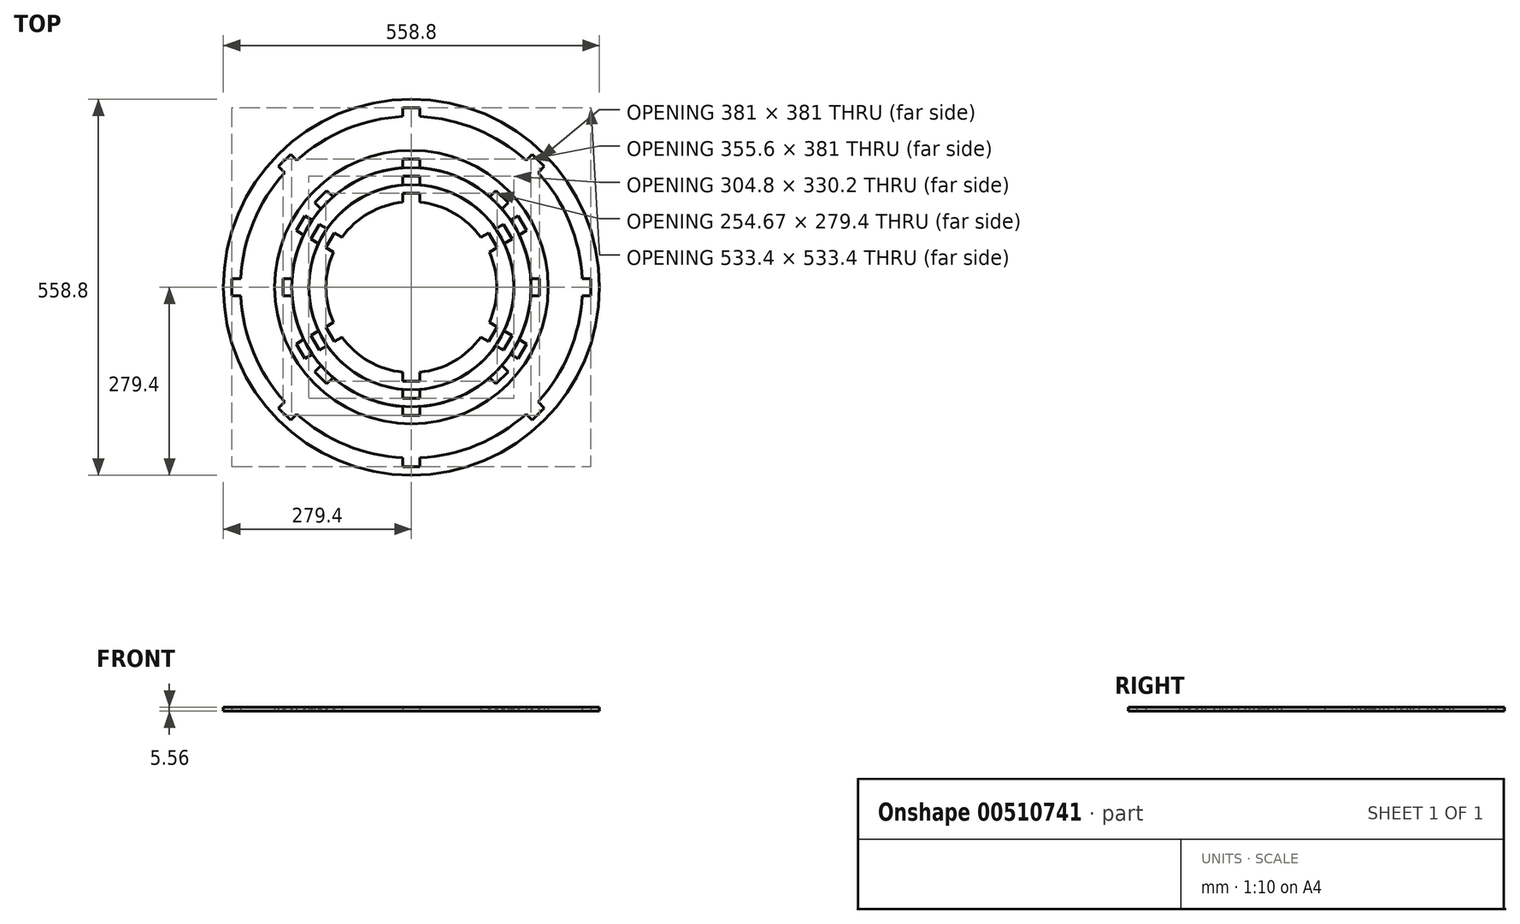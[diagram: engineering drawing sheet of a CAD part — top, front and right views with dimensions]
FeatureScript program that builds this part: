
annotation { "Feature Type Name" : "Feature", "Feature Type Description" : "" }
export const myFeature = defineFeature(function(context is Context, id is Id, definition is map)
    precondition{}
    {
        {
            var Q0;
            Q0=qCreatedBy(makeId("Top.planeOp"),FACE);
            var sketch = newSketch(context, id + "F0", { "sketchPlane" : qUnion([Q0])});
            skCircle(sketch, "E0", {"center": v(0, 0) * mm, "radius": 127 * mm});
            skCircle(sketch, "E1", {"center": v(0, 0) * mm, "radius": 152.4 * mm});
            skCircle(sketch, "E2", {"center": v(0, 0) * mm, "radius": 177.8 * mm});
            skCircle(sketch, "E3.cCircle", {"center": v(0, 0) * mm, "radius": 139.7 * mm, "construction": true});
            skLineSegment(sketch, "E3.0", {"start": v(-80.66, 139.7) * mm, "end": v(80.66, 139.7) * mm, "construction": true});
            skLineSegment(sketch, "E3.1", {"start": v(80.66, 139.7) * mm, "end": v(161.31, 0) * mm, "construction": true});
            skLineSegment(sketch, "E3.2", {"start": v(161.31, 0) * mm, "end": v(80.66, -139.7) * mm, "construction": true});
            skLineSegment(sketch, "E3.4", {"start": v(-80.66, -139.7) * mm, "end": v(-161.31, 0) * mm, "construction": true});
            skLineSegment(sketch, "E3.5", {"start": v(-161.31, 0) * mm, "end": v(-80.66, 139.7) * mm, "construction": true});
            skPoint(sketch, "E3.0.midPoint", {"position": v(0, 139.7) * mm});
            skCircle(sketch, "E4.cCircle", {"center": v(0, 0) * mm, "radius": 165.1 * mm, "construction": true});
            skLineSegment(sketch, "E4.0", {"start": v(-95.32, 165.1) * mm, "end": v(95.32, 165.1) * mm, "construction": true});
            skLineSegment(sketch, "E4.1", {"start": v(95.32, 165.1) * mm, "end": v(190.64, 0) * mm, "construction": true});
            skLineSegment(sketch, "E4.2", {"start": v(190.64, 0) * mm, "end": v(95.32, -165.1) * mm, "construction": true});
            skLineSegment(sketch, "E4.4", {"start": v(-95.32, -165.1) * mm, "end": v(-190.64, 0) * mm, "construction": true});
            skLineSegment(sketch, "E4.5", {"start": v(-190.64, 0) * mm, "end": v(-95.32, 165.1) * mm, "construction": true});
            skPoint(sketch, "E4.0.midPoint", {"position": v(0, 165.1) * mm});
            skCircle(sketch, "E5.cCircle", {"center": v(0, 0) * mm, "radius": 190.5 * mm, "construction": true});
            skLineSegment(sketch, "E5.0", {"start": v(-109.99, 190.5) * mm, "end": v(109.99, 190.5) * mm, "construction": true});
            skLineSegment(sketch, "E5.1", {"start": v(109.99, 190.5) * mm, "end": v(219.97, 0) * mm, "construction": true});
            skLineSegment(sketch, "E5.2", {"start": v(219.97, 0) * mm, "end": v(109.99, -190.5) * mm, "construction": true});
            skLineSegment(sketch, "E5.4", {"start": v(-109.99, -190.5) * mm, "end": v(-219.97, 0) * mm, "construction": true});
            skLineSegment(sketch, "E5.5", {"start": v(-219.97, 0) * mm, "end": v(-109.99, 190.5) * mm, "construction": true});
            skPoint(sketch, "E5.0.midPoint", {"position": v(0, 190.5) * mm});
            skCircle(sketch, "E6", {"center": v(0, 0) * mm, "radius": 203.2 * mm});
            skLineSegment(sketch, "E7", {"start": v(0, 114.9) * mm, "end": v(12.7, 114.9) * mm, "construction": true});
            skLineSegment(sketch, "E8", {"start": v(12.7, 126.36) * mm, "end": v(12.7, 139.7) * mm});
            skLineSegment(sketch, "E9", {"start": v(12.7, 139.7) * mm, "end": v(-12.7, 139.7) * mm});
            skLineSegment(sketch, "E10", {"start": v(-12.7, 139.7) * mm, "end": v(-12.7, 126.36) * mm});
            skLineSegment(sketch, "E11", {"start": v(-12.7, 151.87) * mm, "end": v(-12.7, 164.61) * mm});
            skLineSegment(sketch, "E12", {"start": v(-12.7, 164.61) * mm, "end": v(-12.7, 165.1) * mm});
            skLineSegment(sketch, "E13", {"start": v(-12.7, 165.1) * mm, "end": v(12.7, 165.1) * mm});
            skLineSegment(sketch, "E14", {"start": v(12.7, 165.1) * mm, "end": v(12.7, 151.87) * mm});
            skLineSegment(sketch, "E15", {"start": v(-12.7, 177.35) * mm, "end": v(-12.7, 190.5) * mm});
            skLineSegment(sketch, "E16", {"start": v(-12.7, 190.5) * mm, "end": v(12.7, 190.5) * mm});
            skLineSegment(sketch, "E17", {"start": v(12.7, 190.5) * mm, "end": v(12.7, 177.35) * mm});
            skPoint(sketch, "E18.orphan", {"position": v(-12.7, 120.26) * mm});
            skPoint(sketch, "E19.center", {"position": v(0.37, 0.77) * mm});
            skPoint(sketch, "E20.1.0", {"position": v(-164.98, 95.25) * mm});
            skLineSegment(sketch, "E20.1.1", {"start": v(-159.94, 77.67) * mm, "end": v(-171.33, 84.25) * mm});
            skLineSegment(sketch, "E20.1.2", {"start": v(-103.08, 74.18) * mm, "end": v(-114.63, 80.85) * mm});
            skLineSegment(sketch, "E20.1.3", {"start": v(-171.33, 84.25) * mm, "end": v(-158.63, 106.25) * mm});
            skLineSegment(sketch, "E20.1.4", {"start": v(-149.33, 71.55) * mm, "end": v(-136.63, 93.55) * mm});
            skLineSegment(sketch, "E20.1.5", {"start": v(-127.33, 58.85) * mm, "end": v(-115.78, 52.18) * mm});
            skLineSegment(sketch, "E20.1.6", {"start": v(-136.63, 93.55) * mm, "end": v(-125.17, 86.93) * mm});
            skPoint(sketch, "E20.1.7", {"position": v(-120.98, 69.85) * mm});
            skPoint(sketch, "E20.1.8", {"position": v(-142.98, 82.55) * mm});
            skLineSegment(sketch, "E20.1.9", {"start": v(-137.87, 64.94) * mm, "end": v(-148.9, 71.3) * mm});
            skLineSegment(sketch, "E20.1.10", {"start": v(-114.63, 80.85) * mm, "end": v(-127.33, 58.85) * mm});
            skLineSegment(sketch, "E20.1.11", {"start": v(-158.63, 106.25) * mm, "end": v(-147.24, 99.67) * mm});
            skLineSegment(sketch, "E20.1.12", {"start": v(-148.9, 71.3) * mm, "end": v(-149.33, 71.55) * mm});
            skPoint(sketch, "E20.2.0", {"position": v(-164.98, -95.25) * mm});
            skLineSegment(sketch, "E20.2.1", {"start": v(-147.24, -99.67) * mm, "end": v(-158.63, -106.25) * mm});
            skLineSegment(sketch, "E20.2.2", {"start": v(-115.78, -52.18) * mm, "end": v(-127.33, -58.85) * mm});
            skLineSegment(sketch, "E20.2.3", {"start": v(-158.63, -106.25) * mm, "end": v(-171.33, -84.25) * mm});
            skLineSegment(sketch, "E20.2.4", {"start": v(-136.63, -93.55) * mm, "end": v(-149.33, -71.55) * mm});
            skLineSegment(sketch, "E20.2.5", {"start": v(-114.63, -80.85) * mm, "end": v(-103.08, -74.18) * mm});
            skLineSegment(sketch, "E20.2.6", {"start": v(-149.33, -71.55) * mm, "end": v(-137.87, -64.94) * mm});
            skPoint(sketch, "E20.2.7", {"position": v(-120.98, -69.85) * mm});
            skPoint(sketch, "E20.2.8", {"position": v(-142.98, -82.55) * mm});
            skLineSegment(sketch, "E20.2.9", {"start": v(-125.17, -86.93) * mm, "end": v(-136.2, -93.3) * mm});
            skLineSegment(sketch, "E20.2.10", {"start": v(-127.33, -58.85) * mm, "end": v(-114.63, -80.85) * mm});
            skLineSegment(sketch, "E20.2.11", {"start": v(-171.33, -84.25) * mm, "end": v(-159.94, -77.67) * mm});
            skLineSegment(sketch, "E20.2.12", {"start": v(-136.2, -93.3) * mm, "end": v(-136.63, -93.55) * mm});
            skPoint(sketch, "E20.3.0", {"position": v(0, -190.5) * mm});
            skLineSegment(sketch, "E20.3.1", {"start": v(12.7, -177.35) * mm, "end": v(12.7, -190.5) * mm});
            skLineSegment(sketch, "E20.3.2", {"start": v(-12.7, -126.36) * mm, "end": v(-12.7, -139.7) * mm});
            skLineSegment(sketch, "E20.3.3", {"start": v(12.7, -190.5) * mm, "end": v(-12.7, -190.5) * mm});
            skLineSegment(sketch, "E20.3.4", {"start": v(12.7, -165.1) * mm, "end": v(-12.7, -165.1) * mm});
            skLineSegment(sketch, "E20.3.5", {"start": v(12.7, -139.7) * mm, "end": v(12.7, -126.36) * mm});
            skLineSegment(sketch, "E20.3.6", {"start": v(-12.7, -165.1) * mm, "end": v(-12.7, -151.87) * mm});
            skPoint(sketch, "E20.3.7", {"position": v(0, -139.7) * mm});
            skPoint(sketch, "E20.3.8", {"position": v(0, -165.1) * mm});
            skLineSegment(sketch, "E20.3.9", {"start": v(12.7, -151.87) * mm, "end": v(12.7, -164.61) * mm});
            skLineSegment(sketch, "E20.3.10", {"start": v(-12.7, -139.7) * mm, "end": v(12.7, -139.7) * mm});
            skLineSegment(sketch, "E20.3.11", {"start": v(-12.7, -190.5) * mm, "end": v(-12.7, -177.35) * mm});
            skLineSegment(sketch, "E20.3.12", {"start": v(12.7, -164.61) * mm, "end": v(12.7, -165.1) * mm});
            skPoint(sketch, "E20.4.0", {"position": v(164.98, -95.25) * mm});
            skLineSegment(sketch, "E20.4.1", {"start": v(159.94, -77.67) * mm, "end": v(171.33, -84.25) * mm});
            skLineSegment(sketch, "E20.4.2", {"start": v(103.08, -74.18) * mm, "end": v(114.63, -80.85) * mm});
            skLineSegment(sketch, "E20.4.3", {"start": v(171.33, -84.25) * mm, "end": v(158.63, -106.25) * mm});
            skLineSegment(sketch, "E20.4.4", {"start": v(149.33, -71.55) * mm, "end": v(136.63, -93.55) * mm});
            skLineSegment(sketch, "E20.4.5", {"start": v(127.33, -58.85) * mm, "end": v(115.78, -52.18) * mm});
            skLineSegment(sketch, "E20.4.6", {"start": v(136.63, -93.55) * mm, "end": v(125.17, -86.93) * mm});
            skPoint(sketch, "E20.4.7", {"position": v(120.98, -69.85) * mm});
            skPoint(sketch, "E20.4.8", {"position": v(142.98, -82.55) * mm});
            skLineSegment(sketch, "E20.4.9", {"start": v(137.87, -64.94) * mm, "end": v(148.9, -71.3) * mm});
            skLineSegment(sketch, "E20.4.10", {"start": v(114.63, -80.85) * mm, "end": v(127.33, -58.85) * mm});
            skLineSegment(sketch, "E20.4.11", {"start": v(158.63, -106.25) * mm, "end": v(147.24, -99.67) * mm});
            skLineSegment(sketch, "E20.4.12", {"start": v(148.9, -71.3) * mm, "end": v(149.33, -71.55) * mm});
            skPoint(sketch, "E20.5.0", {"position": v(164.98, 95.25) * mm});
            skLineSegment(sketch, "E20.5.1", {"start": v(147.24, 99.67) * mm, "end": v(158.63, 106.25) * mm});
            skLineSegment(sketch, "E20.5.2", {"start": v(115.78, 52.18) * mm, "end": v(127.33, 58.85) * mm});
            skLineSegment(sketch, "E20.5.3", {"start": v(158.63, 106.25) * mm, "end": v(171.33, 84.25) * mm});
            skLineSegment(sketch, "E20.5.4", {"start": v(136.63, 93.55) * mm, "end": v(149.33, 71.55) * mm});
            skLineSegment(sketch, "E20.5.5", {"start": v(114.63, 80.85) * mm, "end": v(103.08, 74.18) * mm});
            skLineSegment(sketch, "E20.5.6", {"start": v(149.33, 71.55) * mm, "end": v(137.87, 64.94) * mm});
            skPoint(sketch, "E20.5.7", {"position": v(120.98, 69.85) * mm});
            skPoint(sketch, "E20.5.8", {"position": v(142.98, 82.55) * mm});
            skLineSegment(sketch, "E20.5.9", {"start": v(125.17, 86.93) * mm, "end": v(136.2, 93.3) * mm});
            skLineSegment(sketch, "E20.5.10", {"start": v(127.33, 58.85) * mm, "end": v(114.63, 80.85) * mm});
            skLineSegment(sketch, "E20.5.11", {"start": v(171.33, 84.25) * mm, "end": v(159.94, 77.67) * mm});
            skLineSegment(sketch, "E20.5.12", {"start": v(136.2, 93.3) * mm, "end": v(136.63, 93.55) * mm});
            skSolve(sketch);
        }
        {
            var Q0;
            {var subQ17=sQuery(id+"F0.wireOp",EDGE,"E8");Q0=makeQuery(id+"F0.imprint","IMPRINT",FACE,{"disambiguationData":[TD([[makeQuery(id+"F0.imprint","IMPRINT",EDGE,{"derivedFrom":subQ17}),-1.0]])]});}
            var Q1;
            Q1=makeQuery(id+"F0.imprint","IMPRINT",FACE,{"disambiguationData":[TD([[makeQuery(id+"F0.imprint","IMPRINT",EDGE,{"derivedFrom":sQuery(id+"F0.wireOp",EDGE,"E6")}),1.0]])]});
            extrude(context, id + "F1", {"entities" : qUnion([Q0, Q1]), "depth" : 5.56 * mm, "offsetDistance" : 25.4 * mm});
        }
        {
            var Q0;
            {var subQ16=sQuery(id+"F0.wireOp",EDGE,"E11");Q0=makeQuery(id+"F0.imprint","IMPRINT",FACE,{"disambiguationData":[TD([[makeQuery(id+"F0.imprint","IMPRINT",EDGE,{"derivedFrom":subQ16}),1.0]])]});}
            extrude(context, id + "F2", {"entities" : qUnion([Q0]), "depth" : 5.56 * mm, "offsetDistance" : 25.4 * mm});
        }
        {
            var Q0;
            Q0=qCreatedBy(makeId("Top.planeOp"),FACE);
            var sketch = newSketch(context, id + "F3", { "sketchPlane" : qUnion([Q0])});
            skCircle(sketch, "E21", {"center": v(0, 0) * mm, "radius": 177.8 * mm});
            skCircle(sketch, "E22", {"center": v(0, 0) * mm, "radius": 203.2 * mm});
            skCircle(sketch, "E23.cCircle", {"center": v(0, 0) * mm, "radius": 190.5 * mm, "construction": true});
            skLineSegment(sketch, "E23.0", {"start": v(-78.9, 190.5) * mm, "end": v(78.9, 190.5) * mm, "construction": true});
            skLineSegment(sketch, "E23.1", {"start": v(78.9, 190.5) * mm, "end": v(190.5, 78.9) * mm, "construction": true});
            skLineSegment(sketch, "E23.2", {"start": v(190.5, 78.9) * mm, "end": v(190.5, -78.9) * mm, "construction": true});
            skLineSegment(sketch, "E23.3", {"start": v(190.5, -78.9) * mm, "end": v(78.9, -190.5) * mm, "construction": true});
            skLineSegment(sketch, "E23.4", {"start": v(78.9, -190.5) * mm, "end": v(-78.9, -190.5) * mm, "construction": true});
            skLineSegment(sketch, "E23.5", {"start": v(-78.9, -190.5) * mm, "end": v(-190.5, -78.9) * mm, "construction": true});
            skLineSegment(sketch, "E23.6", {"start": v(-190.5, -78.9) * mm, "end": v(-190.5, 78.9) * mm, "construction": true});
            skLineSegment(sketch, "E23.7", {"start": v(-190.5, 78.9) * mm, "end": v(-78.9, 190.5) * mm, "construction": true});
            skPoint(sketch, "E23.0.midPoint", {"position": v(0, 190.5) * mm});
            skLineSegment(sketch, "E24", {"start": v(0, 190.5) * mm, "end": v(12.7, 190.5) * mm});
            skLineSegment(sketch, "E25", {"start": v(12.7, 190.5) * mm, "end": v(12.7, 177.35) * mm});
            skLineSegment(sketch, "E26", {"start": v(0, 190.5) * mm, "end": v(-12.7, 190.5) * mm});
            skLineSegment(sketch, "E27", {"start": v(-12.7, 190.5) * mm, "end": v(-12.7, 177.35) * mm});
            skCircle(sketch, "E28", {"center": v(0, 0) * mm, "radius": 254 * mm});
            skCircle(sketch, "E29", {"center": v(0, 0) * mm, "radius": 279.4 * mm});
            skCircle(sketch, "E30.cCircle", {"center": v(0, 0) * mm, "radius": 266.7 * mm, "construction": true});
            skLineSegment(sketch, "E30.0", {"start": v(-110.47, 266.7) * mm, "end": v(110.47, 266.7) * mm, "construction": true});
            skLineSegment(sketch, "E30.1", {"start": v(110.47, 266.7) * mm, "end": v(266.7, 110.47) * mm, "construction": true});
            skLineSegment(sketch, "E30.2", {"start": v(266.7, 110.47) * mm, "end": v(266.7, -110.47) * mm, "construction": true});
            skLineSegment(sketch, "E30.3", {"start": v(266.7, -110.47) * mm, "end": v(110.47, -266.7) * mm, "construction": true});
            skLineSegment(sketch, "E30.4", {"start": v(110.47, -266.7) * mm, "end": v(-110.47, -266.7) * mm, "construction": true});
            skLineSegment(sketch, "E30.5", {"start": v(-110.47, -266.7) * mm, "end": v(-266.7, -110.47) * mm, "construction": true});
            skLineSegment(sketch, "E30.6", {"start": v(-266.7, -110.47) * mm, "end": v(-266.7, 110.47) * mm, "construction": true});
            skLineSegment(sketch, "E30.7", {"start": v(-266.7, 110.47) * mm, "end": v(-110.47, 266.7) * mm, "construction": true});
            skPoint(sketch, "E30.0.midPoint", {"position": v(0, 266.7) * mm});
            skLineSegment(sketch, "E31", {"start": v(0, 266.7) * mm, "end": v(12.7, 266.7) * mm});
            skLineSegment(sketch, "E32", {"start": v(12.7, 266.7) * mm, "end": v(12.7, 253.68) * mm});
            skLineSegment(sketch, "E33", {"start": v(0, 266.7) * mm, "end": v(-12.7, 266.7) * mm});
            skLineSegment(sketch, "E34", {"start": v(-12.7, 266.7) * mm, "end": v(-12.7, 253.68) * mm});
            skPoint(sketch, "E35.center", {"position": v(0.25, 0.44) * mm});
            skPoint(sketch, "E36.center", {"position": v(0.1, 0.3) * mm});
            skLineSegment(sketch, "E37.1.0", {"start": v(-197.57, 179.6) * mm, "end": v(-188.36, 170.4) * mm});
            skPoint(sketch, "E37.1.1", {"position": v(-188.59, 188.59) * mm});
            skLineSegment(sketch, "E37.1.2", {"start": v(-188.59, 188.59) * mm, "end": v(-179.6, 197.57) * mm});
            skLineSegment(sketch, "E37.1.3", {"start": v(-134.7, 134.7) * mm, "end": v(-125.72, 143.68) * mm});
            skLineSegment(sketch, "E37.1.4", {"start": v(-125.72, 143.68) * mm, "end": v(-116.42, 134.38) * mm});
            skLineSegment(sketch, "E37.1.5", {"start": v(-179.6, 197.57) * mm, "end": v(-170.4, 188.36) * mm});
            skPoint(sketch, "E37.1.6", {"position": v(-134.7, 134.7) * mm});
            skLineSegment(sketch, "E37.1.7", {"start": v(-143.68, 125.72) * mm, "end": v(-134.38, 116.42) * mm});
            skLineSegment(sketch, "E37.1.8", {"start": v(-134.7, 134.7) * mm, "end": v(-143.68, 125.72) * mm});
            skLineSegment(sketch, "E37.1.9", {"start": v(-188.59, 188.59) * mm, "end": v(-197.57, 179.6) * mm});
            skLineSegment(sketch, "E37.2.0", {"start": v(-266.7, -12.7) * mm, "end": v(-253.68, -12.7) * mm});
            skPoint(sketch, "E37.2.1", {"position": v(-266.7, 0) * mm});
            skLineSegment(sketch, "E37.2.2", {"start": v(-266.7, 0) * mm, "end": v(-266.7, 12.7) * mm});
            skLineSegment(sketch, "E37.2.3", {"start": v(-190.5, 0) * mm, "end": v(-190.5, 12.7) * mm});
            skLineSegment(sketch, "E37.2.4", {"start": v(-190.5, 12.7) * mm, "end": v(-177.35, 12.7) * mm});
            skLineSegment(sketch, "E37.2.5", {"start": v(-266.7, 12.7) * mm, "end": v(-253.68, 12.7) * mm});
            skPoint(sketch, "E37.2.6", {"position": v(-190.5, 0) * mm});
            skLineSegment(sketch, "E37.2.7", {"start": v(-190.5, -12.7) * mm, "end": v(-177.35, -12.7) * mm});
            skLineSegment(sketch, "E37.2.8", {"start": v(-190.5, 0) * mm, "end": v(-190.5, -12.7) * mm});
            skLineSegment(sketch, "E37.2.9", {"start": v(-266.7, 0) * mm, "end": v(-266.7, -12.7) * mm});
            skLineSegment(sketch, "E37.3.0", {"start": v(-179.6, -197.57) * mm, "end": v(-170.4, -188.36) * mm});
            skPoint(sketch, "E37.3.1", {"position": v(-188.59, -188.59) * mm});
            skLineSegment(sketch, "E37.3.2", {"start": v(-188.59, -188.59) * mm, "end": v(-197.57, -179.6) * mm});
            skLineSegment(sketch, "E37.3.3", {"start": v(-134.7, -134.7) * mm, "end": v(-143.68, -125.72) * mm});
            skLineSegment(sketch, "E37.3.4", {"start": v(-143.68, -125.72) * mm, "end": v(-134.38, -116.42) * mm});
            skLineSegment(sketch, "E37.3.5", {"start": v(-197.57, -179.6) * mm, "end": v(-188.36, -170.4) * mm});
            skPoint(sketch, "E37.3.6", {"position": v(-134.7, -134.7) * mm});
            skLineSegment(sketch, "E37.3.7", {"start": v(-125.72, -143.68) * mm, "end": v(-116.42, -134.38) * mm});
            skLineSegment(sketch, "E37.3.8", {"start": v(-134.7, -134.7) * mm, "end": v(-125.72, -143.68) * mm});
            skLineSegment(sketch, "E37.3.9", {"start": v(-188.59, -188.59) * mm, "end": v(-179.6, -197.57) * mm});
            skLineSegment(sketch, "E37.4.0", {"start": v(12.7, -266.7) * mm, "end": v(12.7, -253.68) * mm});
            skPoint(sketch, "E37.4.1", {"position": v(0, -266.7) * mm});
            skLineSegment(sketch, "E37.4.2", {"start": v(0, -266.7) * mm, "end": v(-12.7, -266.7) * mm});
            skLineSegment(sketch, "E37.4.3", {"start": v(0, -190.5) * mm, "end": v(-12.7, -190.5) * mm});
            skLineSegment(sketch, "E37.4.4", {"start": v(-12.7, -190.5) * mm, "end": v(-12.7, -177.35) * mm});
            skLineSegment(sketch, "E37.4.5", {"start": v(-12.7, -266.7) * mm, "end": v(-12.7, -253.68) * mm});
            skPoint(sketch, "E37.4.6", {"position": v(0, -190.5) * mm});
            skLineSegment(sketch, "E37.4.7", {"start": v(12.7, -190.5) * mm, "end": v(12.7, -177.35) * mm});
            skLineSegment(sketch, "E37.4.8", {"start": v(0, -190.5) * mm, "end": v(12.7, -190.5) * mm});
            skLineSegment(sketch, "E37.4.9", {"start": v(0, -266.7) * mm, "end": v(12.7, -266.7) * mm});
            skLineSegment(sketch, "E37.5.0", {"start": v(197.57, -179.6) * mm, "end": v(188.36, -170.4) * mm});
            skPoint(sketch, "E37.5.1", {"position": v(188.59, -188.59) * mm});
            skLineSegment(sketch, "E37.5.2", {"start": v(188.59, -188.59) * mm, "end": v(179.6, -197.57) * mm});
            skLineSegment(sketch, "E37.5.3", {"start": v(134.7, -134.7) * mm, "end": v(125.72, -143.68) * mm});
            skLineSegment(sketch, "E37.5.4", {"start": v(125.72, -143.68) * mm, "end": v(116.42, -134.38) * mm});
            skLineSegment(sketch, "E37.5.5", {"start": v(179.6, -197.57) * mm, "end": v(170.4, -188.36) * mm});
            skPoint(sketch, "E37.5.6", {"position": v(134.7, -134.7) * mm});
            skLineSegment(sketch, "E37.5.7", {"start": v(143.68, -125.72) * mm, "end": v(134.38, -116.42) * mm});
            skLineSegment(sketch, "E37.5.8", {"start": v(134.7, -134.7) * mm, "end": v(143.68, -125.72) * mm});
            skLineSegment(sketch, "E37.5.9", {"start": v(188.59, -188.59) * mm, "end": v(197.57, -179.6) * mm});
            skLineSegment(sketch, "E37.6.0", {"start": v(266.7, 12.7) * mm, "end": v(253.68, 12.7) * mm});
            skPoint(sketch, "E37.6.1", {"position": v(266.7, 0) * mm});
            skLineSegment(sketch, "E37.6.2", {"start": v(266.7, 0) * mm, "end": v(266.7, -12.7) * mm});
            skLineSegment(sketch, "E37.6.3", {"start": v(190.5, 0) * mm, "end": v(190.5, -12.7) * mm});
            skLineSegment(sketch, "E37.6.4", {"start": v(190.5, -12.7) * mm, "end": v(177.35, -12.7) * mm});
            skLineSegment(sketch, "E37.6.5", {"start": v(266.7, -12.7) * mm, "end": v(253.68, -12.7) * mm});
            skPoint(sketch, "E37.6.6", {"position": v(190.5, 0) * mm});
            skLineSegment(sketch, "E37.6.7", {"start": v(190.5, 12.7) * mm, "end": v(177.35, 12.7) * mm});
            skLineSegment(sketch, "E37.6.8", {"start": v(190.5, 0) * mm, "end": v(190.5, 12.7) * mm});
            skLineSegment(sketch, "E37.6.9", {"start": v(266.7, 0) * mm, "end": v(266.7, 12.7) * mm});
            skLineSegment(sketch, "E37.7.0", {"start": v(179.6, 197.57) * mm, "end": v(170.4, 188.36) * mm});
            skPoint(sketch, "E37.7.1", {"position": v(188.59, 188.59) * mm});
            skLineSegment(sketch, "E37.7.2", {"start": v(188.59, 188.59) * mm, "end": v(197.57, 179.6) * mm});
            skLineSegment(sketch, "E37.7.3", {"start": v(134.7, 134.7) * mm, "end": v(143.68, 125.72) * mm});
            skLineSegment(sketch, "E37.7.4", {"start": v(143.68, 125.72) * mm, "end": v(134.38, 116.42) * mm});
            skLineSegment(sketch, "E37.7.5", {"start": v(197.57, 179.6) * mm, "end": v(188.36, 170.4) * mm});
            skPoint(sketch, "E37.7.6", {"position": v(134.7, 134.7) * mm});
            skLineSegment(sketch, "E37.7.7", {"start": v(125.72, 143.68) * mm, "end": v(116.42, 134.38) * mm});
            skLineSegment(sketch, "E37.7.8", {"start": v(134.7, 134.7) * mm, "end": v(125.72, 143.68) * mm});
            skLineSegment(sketch, "E37.7.9", {"start": v(188.59, 188.59) * mm, "end": v(179.6, 197.57) * mm});
            skSolve(sketch);
        }
        {
            var Q0;
            Q0=makeQuery(id+"F3.imprint","IMPRINT",FACE,{"disambiguationData":[TD([[makeQuery(id+"F3.imprint","IMPRINT",EDGE,{"derivedFrom":sQuery(id+"F3.wireOp",EDGE,"E22")}),1.0]])]});
            var Q1;
            Q1=makeQuery(id+"F3.imprint","IMPRINT",FACE,{"disambiguationData":[TD([[makeQuery(id+"F3.imprint","IMPRINT",EDGE,{"derivedFrom":sQuery(id+"F3.wireOp",EDGE,"E29")}),1.0]])]});
            extrude(context, id + "F4", {"entities" : qUnion([Q0, Q1]), "depth" : 5.56 * mm, "offsetDistance" : 25.4 * mm});
        }
    });
